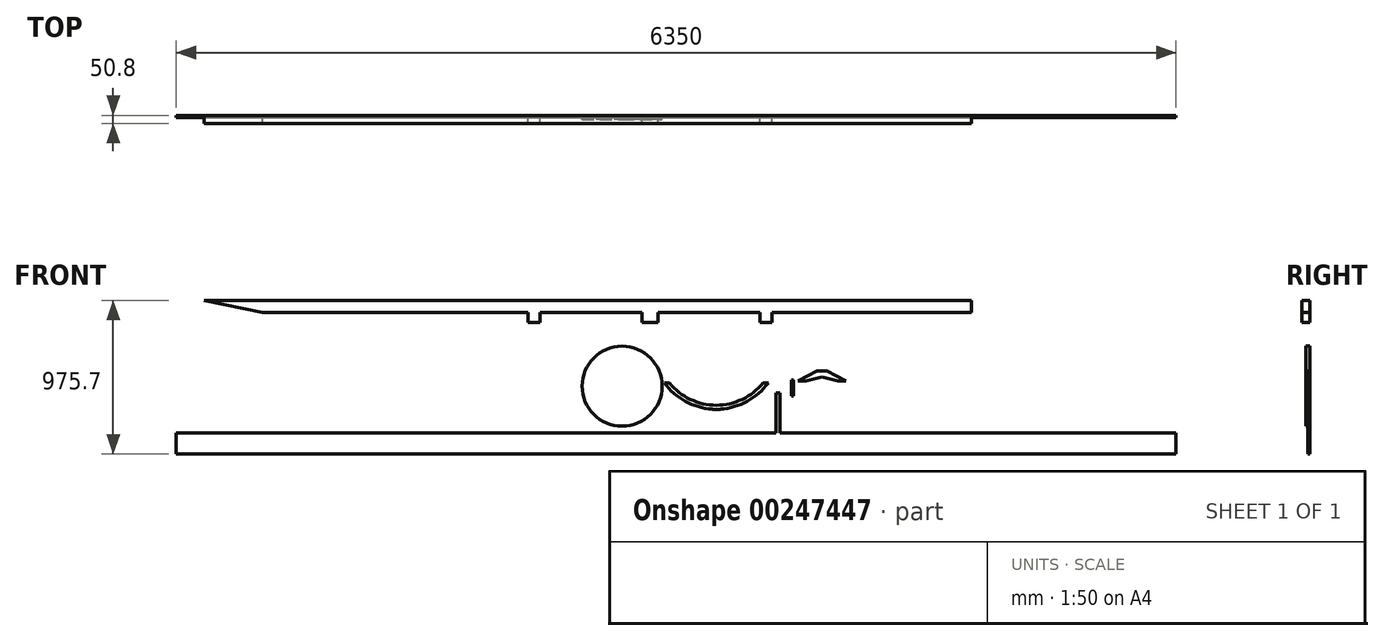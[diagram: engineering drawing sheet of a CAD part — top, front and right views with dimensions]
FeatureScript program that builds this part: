
annotation { "Feature Type Name" : "Feature", "Feature Type Description" : "" }
export const myFeature = defineFeature(function(context is Context, id is Id, definition is map)
    precondition{}
    {
        {
            var Q0;
            Q0=qCreatedBy(makeId("Front.planeOp"),FACE);
            var sketch = newSketch(context, id + "F0", { "sketchPlane" : qUnion([Q0])});
            skLineSegment(sketch, "E0.top", {"start": v(-698.5, 317.5) * mm, "end": v(-50.8, 317.5) * mm});
            skLineSegment(sketch, "E0.left", {"start": v(-774.7, 317.5) * mm, "end": v(-774.7, 317.5) * mm});
            skLineSegment(sketch, "E0.right", {"start": v(774.7, 317.5) * mm, "end": v(774.7, 317.5) * mm});
            skLineSegment(sketch, "E1.top", {"start": v(-774.7, 254) * mm, "end": v(-698.5, 254) * mm});
            skLineSegment(sketch, "E1.left", {"start": v(-774.7, 317.5) * mm, "end": v(-774.7, 254) * mm});
            skLineSegment(sketch, "E1.right", {"start": v(-698.5, 317.5) * mm, "end": v(-698.5, 254) * mm});
            skLineSegment(sketch, "E2.top", {"start": v(-50.8, 254) * mm, "end": v(50.8, 254) * mm});
            skLineSegment(sketch, "E2.left", {"start": v(-50.8, 317.5) * mm, "end": v(-50.8, 254) * mm});
            skLineSegment(sketch, "E2.right", {"start": v(50.8, 317.5) * mm, "end": v(50.8, 254) * mm});
            skLineSegment(sketch, "E3.top", {"start": v(774.7, 254) * mm, "end": v(698.5, 254) * mm});
            skLineSegment(sketch, "E3.left", {"start": v(774.7, 317.5) * mm, "end": v(774.7, 254) * mm});
            skLineSegment(sketch, "E3.right", {"start": v(698.5, 317.5) * mm, "end": v(698.5, 254) * mm});
            skLineSegment(sketch, "E4.trimOffspring", {"start": v(50.8, 317.5) * mm, "end": v(698.5, 317.5) * mm});
            skLineSegment(sketch, "E5", {"start": v(0, 254) * mm, "end": v(0, 0) * mm, "construction": true});
            skLineSegment(sketch, "E6.bottom", {"start": v(-2832.1, 393.7) * mm, "end": v(2044.7, 393.7) * mm});
            skLineSegment(sketch, "E6.top", {"start": v(-2458.8, 317.5) * mm, "end": v(-774.7, 317.5) * mm});
            skLineSegment(sketch, "E6.right", {"start": v(2044.7, 393.7) * mm, "end": v(2044.7, 317.5) * mm});
            skLineSegment(sketch, "E7.trimOffspring", {"start": v(774.7, 317.5) * mm, "end": v(2044.7, 317.5) * mm});
            skLineSegment(sketch, "E8", {"start": v(736.6, 254) * mm, "end": v(736.6, 201.45) * mm, "construction": true});
            skPoint(sketch, "E8.endSnap0", {"position": v(736.6, 254) * mm});
            skLineSegment(sketch, "E9", {"start": v(-736.6, 254) * mm, "end": v(-736.6, 192.81) * mm, "construction": true});
            skLineSegment(sketch, "E10", {"start": v(-2832.1, 393.7) * mm, "end": v(-2458.8, 317.5) * mm});
            skSolve(sketch);
        }
        {
            var Q0;
            Q0 = qSketchRegion(id + "F0", true);
            extrude(context, id + "F1", {"entities" : qUnion([Q0]), "depth" : 50.8 * mm});
        }
        {
            var Q0;
            Q0=qCreatedBy(makeId("Front.planeOp"),FACE);
            var sketch = newSketch(context, id + "F2", { "sketchPlane" : qUnion([Q0]), "disableImprinting" : false});
            skLineSegment(sketch, "E11.bottom", {"start": v(901.29, -112.49) * mm, "end": v(913.99, -112.49) * mm});
            skLineSegment(sketch, "E11.top", {"start": v(901.29, -214.09) * mm, "end": v(913.99, -214.09) * mm});
            skLineSegment(sketch, "E11.left", {"start": v(901.29, -112.49) * mm, "end": v(901.29, -214.09) * mm});
            skLineSegment(sketch, "E11.right", {"start": v(913.99, -112.49) * mm, "end": v(913.99, -214.09) * mm});
            skText(sketch, "E12", { "text": "Original 2.5\"  \nCorrected 3.5-4\"", "fontName": "OpenSans-Regular.ttf"});
            const initialGuessF2  = {"E12": [0.7579, 0.06531, 1, 0, 0.0508]};
            skSetInitialGuess(sketch, initialGuessF2);
            skSolve(sketch);
        }
        {
            var Q0;
            Q0=makeQuery(id+"F2.imprint","IMPRINT",FACE,{"disambiguationData":[TD([[makeQuery(id+"F2.imprint","IMPRINT",EDGE,{"derivedFrom":sQuery(id+"F2.wireOp",EDGE,"E11.bottom")}),-1.0]])]});
            extrude(context, id + "F3", {"entities" : qUnion([Q0]), "depth" : 12.7 * mm});
        }
        {
            var Q0;
            Q0=qCreatedBy(makeId("Front.planeOp"),FACE);
            var sketch = newSketch(context, id + "F4", { "sketchPlane" : qUnion([Q0])});
            skArc(sketch, "E13", {"start": v(92.1, -128.62) * mm, "mid": v(225.76, -246.5) * mm, "end": v(396.9, -296.18) * mm});
            skArc(sketch, "E14.0", {"start": v(124.06, -128.62) * mm, "mid": v(422.3, -271.57) * mm, "end": v(720.55, -128.62) * mm});
            skLineSegment(sketch, "E15", {"start": v(92.1, -128.62) * mm, "end": v(124.06, -128.62) * mm});
            skLineSegment(sketch, "E16", {"start": v(720.55, -128.62) * mm, "end": v(752.5, -128.62) * mm});
            skLineSegment(sketch, "E17", {"start": v(124.06, -128.62) * mm, "end": v(720.55, -128.62) * mm, "construction": true});
            skLineSegment(sketch, "E18", {"start": v(422.3, -128.62) * mm, "end": v(422.3, -259.94) * mm, "construction": true});
            skLineSegment(sketch, "E19.top", {"start": v(396.9, -298.72) * mm, "end": v(447.7, -298.72) * mm});
            skLineSegment(sketch, "E19.left", {"start": v(396.9, -296.18) * mm, "end": v(396.9, -298.72) * mm});
            skLineSegment(sketch, "E19.right", {"start": v(447.7, -296.18) * mm, "end": v(447.7, -298.72) * mm});
            skArc(sketch, "E20.trimOffspring", {"start": v(447.7, -296.18) * mm, "mid": v(618.86, -246.5) * mm, "end": v(752.5, -128.62) * mm});
            skSolve(sketch);
        }
        {
            var Q0;
            Q0=makeQuery(id+"F4.imprint","IMPRINT",FACE,{"disambiguationData":[TD([[makeQuery(id+"F4.imprint","IMPRINT",EDGE,{"derivedFrom":sQuery(id+"F4.wireOp",EDGE,"E13")}),1.0]])]});
            extrude(context, id + "F5", {"entities" : qUnion([Q0]), "depth" : 12.7 * mm});
        }
        {
            var Q0;
            Q0=qCreatedBy(makeId("Front.planeOp"),FACE);
            var sketch = newSketch(context, id + "F6", { "sketchPlane" : qUnion([Q0]), "disableImprinting" : false});
            skLineSegment(sketch, "E21.bottom", {"start": v(1063.34, -54.68) * mm, "end": v(1126.84, -54.68) * mm});
            skLineSegment(sketch, "E21.top", {"start": v(942.69, -118.18) * mm, "end": v(993.49, -118.18) * mm});
            skLineSegment(sketch, "E22", {"start": v(993.49, -118.18) * mm, "end": v(1095.09, -92.78) * mm});
            skLineSegment(sketch, "E23", {"start": v(1095.09, -92.78) * mm, "end": v(1196.69, -118.18) * mm});
            skLineSegment(sketch, "E24", {"start": v(942.69, -118.18) * mm, "end": v(1063.34, -54.68) * mm});
            skLineSegment(sketch, "E25", {"start": v(1247.49, -118.18) * mm, "end": v(1126.84, -54.68) * mm});
            skLineSegment(sketch, "E26.trimOffspring", {"start": v(1196.69, -118.18) * mm, "end": v(1247.49, -118.18) * mm});
            skText(sketch, "E27", { "text": "Original 10\"", "fontName": "OpenSans-Regular.ttf"});
            const initialGuessF6  = {"E27": [0.99176, -0.32136, 1, 0, 0.05161]};
            skSetInitialGuess(sketch, initialGuessF6);
            skSolve(sketch);
        }
        {
            var Q0;
            Q0=makeQuery(id+"F6.imprint","IMPRINT",FACE,{"disambiguationData":[TD([[makeQuery(id+"F6.imprint","IMPRINT",EDGE,{"derivedFrom":sQuery(id+"F6.wireOp",EDGE,"E21.bottom")}),-1.0]])]});
            extrude(context, id + "F7", {"entities" : qUnion([Q0]), "depth" : 12.7 * mm});
        }
        {
            var Q0;
            Q0=qCreatedBy(makeId("Front.planeOp"),FACE);
            var sketch = newSketch(context, id + "F8", { "sketchPlane" : qUnion([Q0])});
            skCircle(sketch, "E28", {"center": v(-175.7, -150.56) * mm, "radius": 254 * mm});
            skSolve(sketch);
        }
        {
            var Q0;
            Q0=makeQuery(id+"F8.imprint","IMPRINT",FACE,{"disambiguationData":[TD([[makeQuery(id+"F8.imprint","IMPRINT",EDGE,{"derivedFrom":sQuery(id+"F8.wireOp",EDGE,"E28")}),1.0]])]});
            extrude(context, id + "F9", {"entities" : qUnion([Q0]), "depth" : 25.4 * mm});
        }
        {
            var Q0;
            Q0=qCreatedBy(makeId("Front.planeOp"),FACE);
            var sketch = newSketch(context, id + "F10", { "sketchPlane" : qUnion([Q0])});
            skLineSegment(sketch, "E29.bottom", {"start": v(-3007.53, -449) * mm, "end": v(802.47, -449) * mm});
            skLineSegment(sketch, "E29.top", {"start": v(-3007.53, -582) * mm, "end": v(3342.47, -582) * mm});
            skLineSegment(sketch, "E29.left", {"start": v(-3007.53, -449) * mm, "end": v(-3007.53, -582) * mm});
            skLineSegment(sketch, "E29.right", {"start": v(3342.47, -449) * mm, "end": v(3342.47, -582) * mm});
            skLineSegment(sketch, "E30.bottom", {"start": v(802.47, -195) * mm, "end": v(827.87, -195) * mm});
            skLineSegment(sketch, "E30.top", {"start": v(802.47, -582) * mm, "end": v(827.87, -582) * mm});
            skLineSegment(sketch, "E30.left", {"start": v(802.47, -195) * mm, "end": v(802.47, -449) * mm});
            skLineSegment(sketch, "E30.right", {"start": v(827.87, -195) * mm, "end": v(827.87, -449) * mm});
            skLineSegment(sketch, "E31.trimOffspring", {"start": v(827.87, -449) * mm, "end": v(3342.47, -449) * mm});
            skSolve(sketch);
        }
        {
            var Q0;
            Q0=makeQuery(id+"F10.imprint","IMPRINT",FACE,{"disambiguationData":[TD([[makeQuery(id+"F10.imprint","IMPRINT",EDGE,{"derivedFrom":sQuery(id+"F10.wireOp",EDGE,"E29.bottom")}),-1.0]])]});
            extrude(context, id + "F11", {"entities" : qUnion([Q0]), "depth" : 12.7 * mm});
        }
    });
